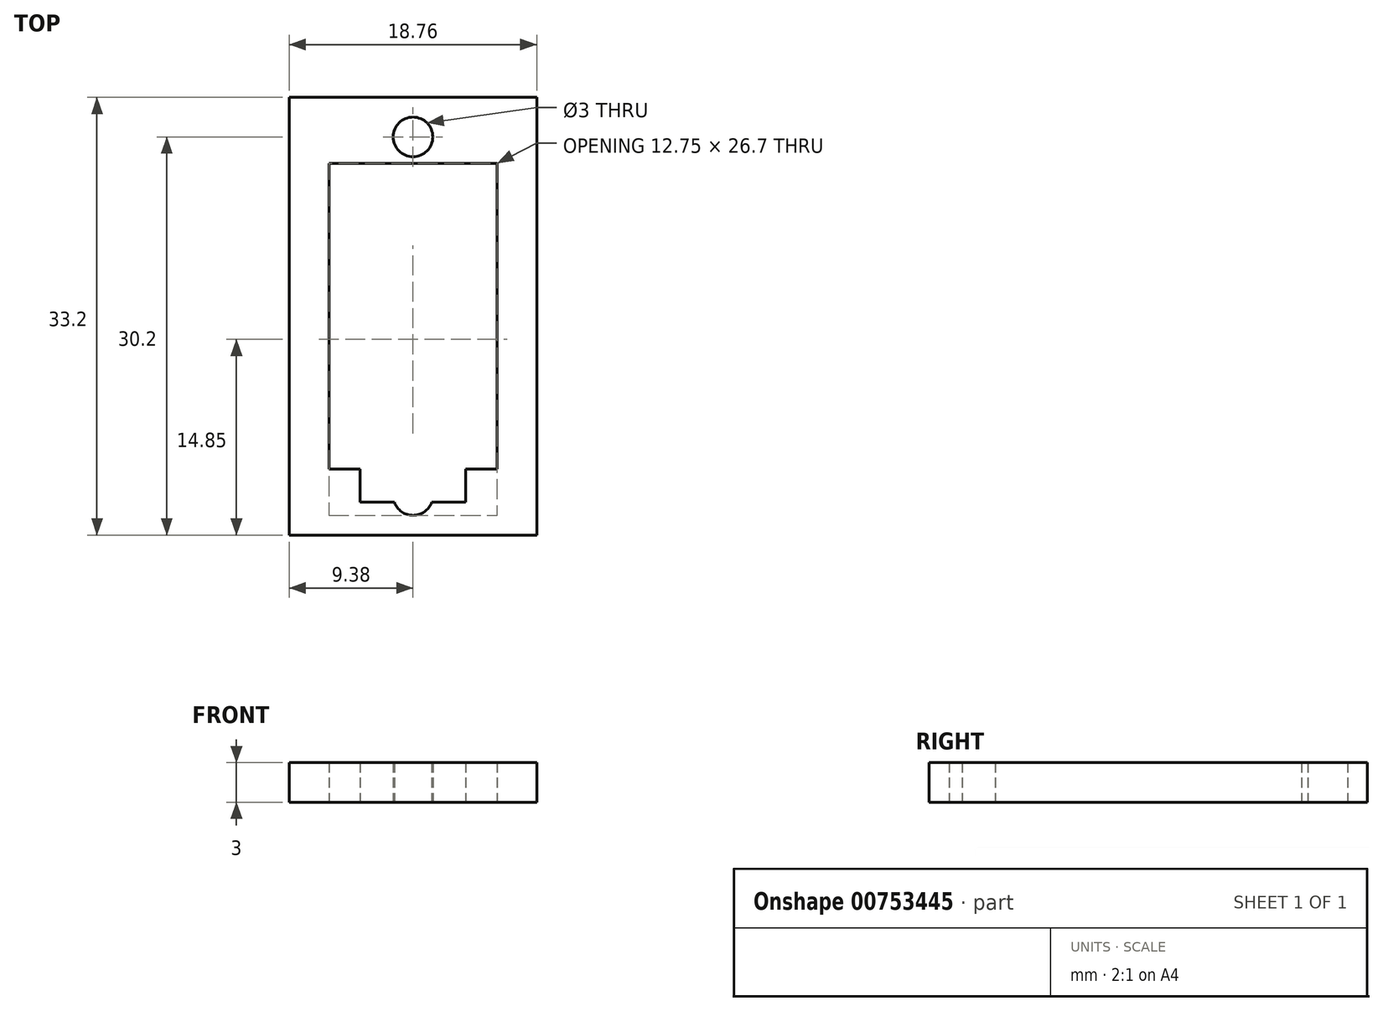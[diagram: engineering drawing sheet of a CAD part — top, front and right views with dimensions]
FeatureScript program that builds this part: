
annotation { "Feature Type Name" : "Feature", "Feature Type Description" : "" }
export const myFeature = defineFeature(function(context is Context, id is Id, definition is map)
    precondition{}
    {
        {
            var Q0;
            Q0=qCreatedBy(makeId("Top.planeOp"),FACE);
            var sketch = newSketch(context, id + "F0", { "sketchPlane" : qUnion([Q0])});
            skLineSegment(sketch, "E0.bottom", {"start": v(-6.38, 11.6) * mm, "end": v(6.37, 11.6) * mm});
            skLineSegment(sketch, "E0.top", {"start": v(-6.38, -11.6) * mm, "end": v(6.37, -11.6) * mm});
            skLineSegment(sketch, "E0.left", {"start": v(-6.38, 11.6) * mm, "end": v(-6.38, -11.6) * mm});
            skLineSegment(sketch, "E0.right", {"start": v(6.38, 11.6) * mm, "end": v(6.38, -11.6) * mm});
            skCircle(sketch, "E1", {"center": v(0, 13.6) * mm, "radius": 1.5 * mm});
            skCircle(sketch, "E2", {"center": v(0, -13.6) * mm, "radius": 1.5 * mm});
            skLineSegment(sketch, "E3.bottom", {"start": v(-9.38, 16.6) * mm, "end": v(9.38, 16.6) * mm});
            skLineSegment(sketch, "E3.top", {"start": v(-9.38, -16.6) * mm, "end": v(9.38, -16.6) * mm});
            skLineSegment(sketch, "E3.left", {"start": v(-9.38, 16.6) * mm, "end": v(-9.38, -16.6) * mm});
            skLineSegment(sketch, "E3.right", {"start": v(9.38, 16.6) * mm, "end": v(9.38, -16.6) * mm});
            skLineSegment(sketch, "E4.bottom", {"start": v(-4, -11.6) * mm, "end": v(4, -11.6) * mm});
            skLineSegment(sketch, "E4.top", {"start": v(-4, -14.1) * mm, "end": v(4, -14.1) * mm});
            skLineSegment(sketch, "E4.left", {"start": v(-4, -11.6) * mm, "end": v(-4, -14.1) * mm});
            skLineSegment(sketch, "E4.right", {"start": v(4, -11.6) * mm, "end": v(4, -14.1) * mm});
            skSolve(sketch);
        }
        {
            var Q0;
            Q0=makeQuery(id+"F0.imprint","IMPRINT",FACE,{"disambiguationData":[TD([[makeQuery(id+"F0.imprint","IMPRINT",EDGE,{"derivedFrom":sQuery(id+"F0.wireOp",EDGE,"E0.bottom")}),1.0]])]});
            extrude(context, id + "F1", {"entities" : qUnion([Q0]), "depth" : 3 * mm, "offsetDistance" : 25 * mm});
        }
    });
